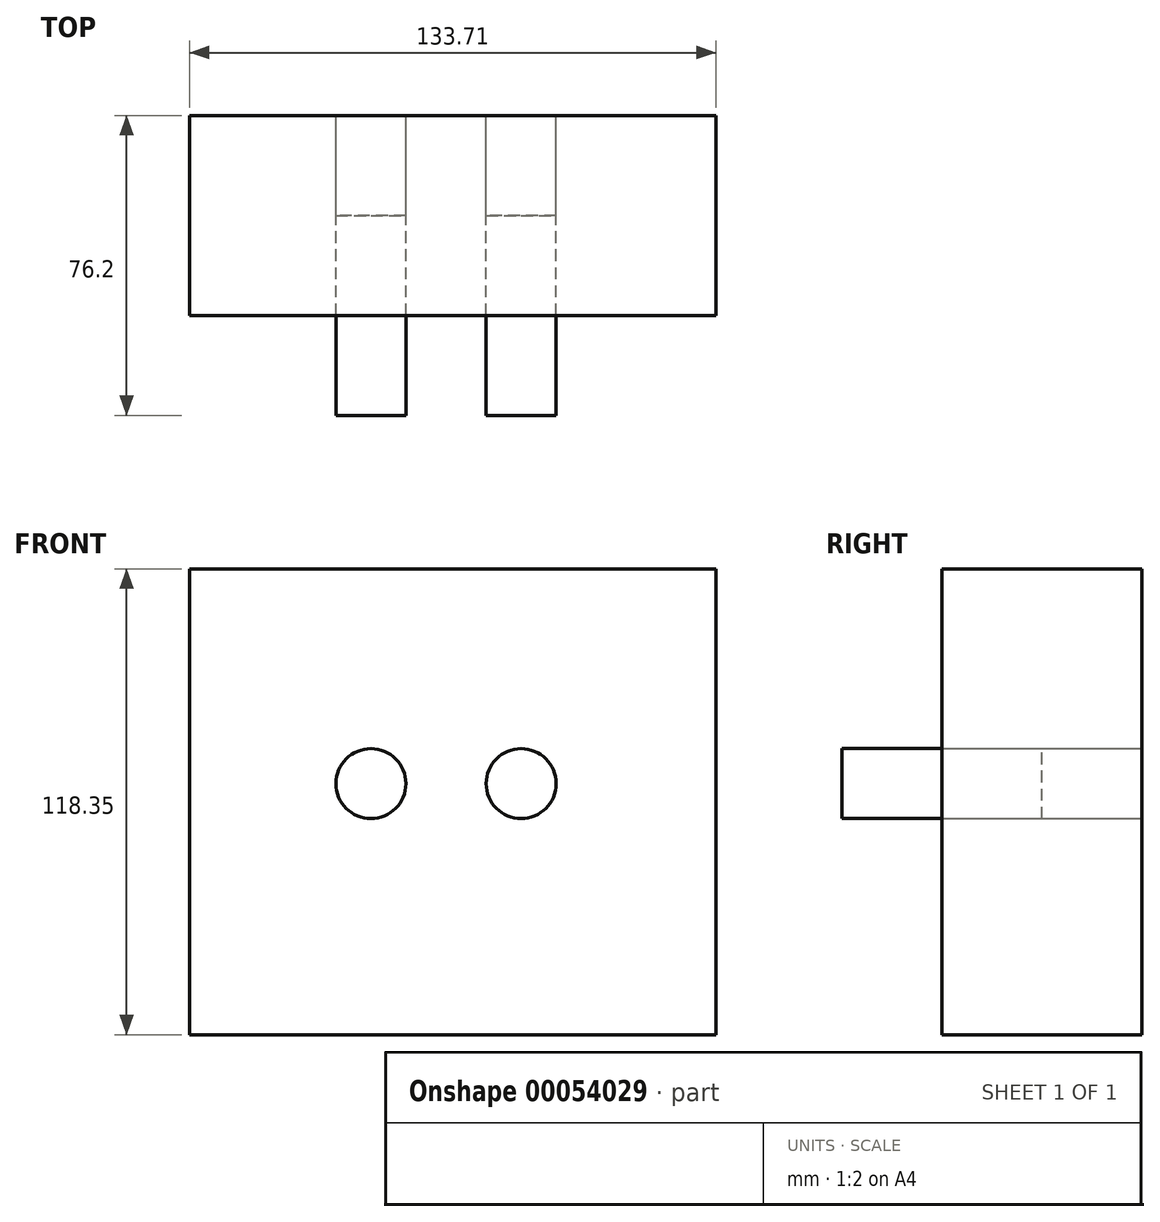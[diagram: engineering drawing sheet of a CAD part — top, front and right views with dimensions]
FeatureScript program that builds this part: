
annotation { "Feature Type Name" : "Feature", "Feature Type Description" : "" }
export const myFeature = defineFeature(function(context is Context, id is Id, definition is map)
    precondition{}
    {
        {
            var Q0;
            Q0=qCreatedBy(makeId("Front.planeOp"),FACE);
            var sketch = newSketch(context, id + "F0", { "sketchPlane" : qUnion([Q0])});
            skLineSegment(sketch, "E0.bottom", {"start": v(-65.12, 54.57) * mm, "end": v(68.59, 54.57) * mm});
            skLineSegment(sketch, "E0.top", {"start": v(-65.12, -63.78) * mm, "end": v(68.59, -63.78) * mm});
            skLineSegment(sketch, "E0.left", {"start": v(-65.12, 54.57) * mm, "end": v(-65.12, -63.78) * mm});
            skLineSegment(sketch, "E0.right", {"start": v(68.59, 54.57) * mm, "end": v(68.59, -63.78) * mm});
            skSolve(sketch);
        }
        {
            var Q0;
            Q0=makeQuery(id+"F0.imprint","IMPRINT",FACE,{"disambiguationData":[TD([[makeQuery(id+"F0.imprint","IMPRINT",EDGE,{"derivedFrom":sQuery(id+"F0.wireOp",EDGE,"E0.bottom")}),-1.0]])]});
            var sketch = newSketch(context, id + "F1", { "sketchPlane" : qUnion([Q0])});
            skLineSegment(sketch, "E1", {"start": v(-19.05, 26.4) * mm, "end": v(-19.05, -35.48) * mm, "construction": true});
            skLineSegment(sketch, "E2", {"start": v(19.1, 26.51) * mm, "end": v(19.1, -36.41) * mm, "construction": true});
            skCircle(sketch, "E3", {"center": v(-19.05, 0) * mm, "radius": 8.9 * mm});
            skCircle(sketch, "E4", {"center": v(19.1, 0) * mm, "radius": 8.9 * mm});
            skSolve(sketch);
        }
        {
            var Q0;
            Q0 = qSketchRegion(id + "F1", true);
            var Q1;
            Q1=makeQuery(id+"F0.imprint","IMPRINT",FACE,{"disambiguationData":[TD([[makeQuery(id+"F0.imprint","IMPRINT",EDGE,{"derivedFrom":sQuery(id+"F0.wireOp",EDGE,"E0.bottom")}),-1.0]])]});
            extrude(context, id + "F2", {"entities" : qUnion([Q0, Q1]), "depth" : 50.8 * mm});
        }
        {
            var Q0;
            Q0 = qSketchRegion(id + "F1", true);
            extrude(context, id + "F3", {"entities" : qUnion([Q0]), "depth" : 25.4 * mm});
        }
        {
            var Q0;
            Q0 = qSketchRegion(id + "F1", true);
            extrude(context, id + "F4", {"entities" : qUnion([Q0]), "depth" : 76.2 * mm});
        }
    });
